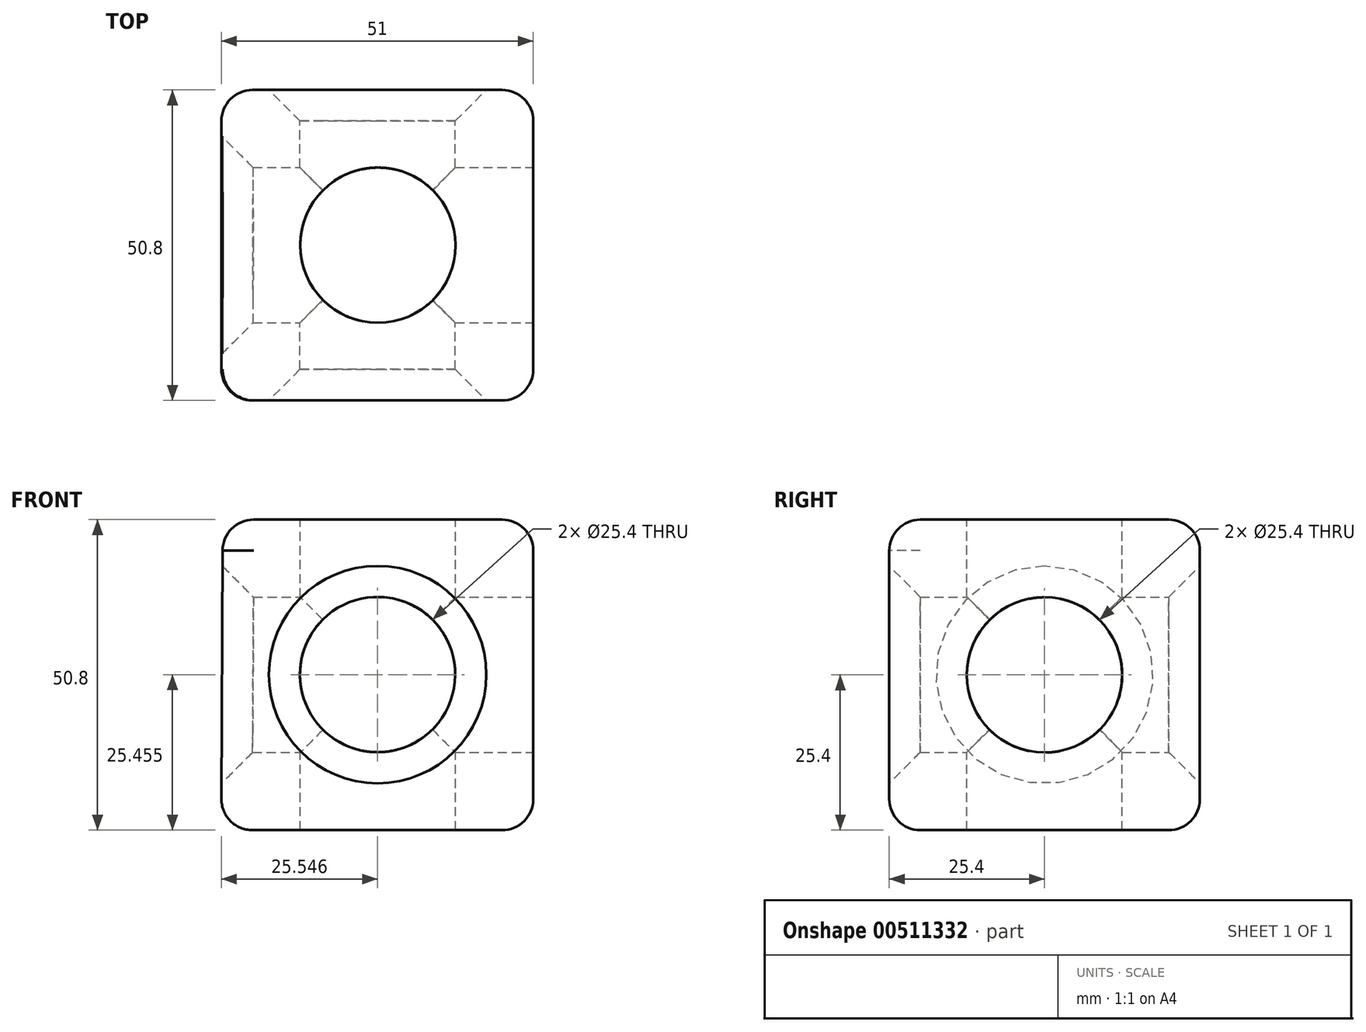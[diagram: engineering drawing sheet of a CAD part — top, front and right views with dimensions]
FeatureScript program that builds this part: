
annotation { "Feature Type Name" : "Feature", "Feature Type Description" : "" }
export const myFeature = defineFeature(function(context is Context, id is Id, definition is map)
    precondition{}
    {
        {
            var Q0;
            Q0=qCreatedBy(makeId("Front.planeOp"),FACE);
            var sketch = newSketch(context, id + "F0", { "sketchPlane" : qUnion([Q0])});
            skLineSegment(sketch, "E0", {"start": v(0, 0) * mm, "end": v(51.02, 0) * mm});
            skLineSegment(sketch, "E1", {"start": v(51.02, 0) * mm, "end": v(51.02, 50.8) * mm});
            skLineSegment(sketch, "E2", {"start": v(51.02, 50.8) * mm, "end": v(0.22, 50.8) * mm});
            skLineSegment(sketch, "E3", {"start": v(0.22, 50.8) * mm, "end": v(0, 0) * mm});
            skCircle(sketch, "E4", {"center": v(25.57, 25.46) * mm, "radius": 12.7 * mm});
            skSolve(sketch);
        }
        {
            var Q0;
            Q0 = qSketchRegion(id + "F0", true);
            extrude(context, id + "F1", {"entities" : qUnion([Q0]), "depth" : 50.8 * mm, "offsetDistance" : 25.4 * mm});
        }
        {
            var Q0;
            Q0=makeQuery(id+"F1.opExtrude","SWEPT_FACE",FACE,{"disambiguationData":[OSD([sQuery(id+"F0.wireOp",EDGE,"E2")])]});
            var sketch = newSketch(context, id + "F2", { "sketchPlane" : qUnion([Q0])});
            skCircle(sketch, "E5", {"center": v(25.62, -25.4) * mm, "radius": 12.7 * mm});
            skPoint(sketch, "E5.centerSnap0", {"position": v(51.02, -25.4) * mm});
            skPoint(sketch, "E5.centerSnap1", {"position": v(25.62, 0) * mm});
            skSolve(sketch);
        }
        {
            var Q0;
            Q0 = qSketchRegion(id + "F2", true);
            extrude(context, id + "F3", {"entities" : qUnion([Q0]), "operationType" : NewBodyOperationType.REMOVE, "oppositeDirection" : true, "depth" : 50.8 * mm, "offsetDistance" : 25.4 * mm});
        }
        {
            var Q0;
            Q0=makeQuery(id+"F1.opExtrude","SWEPT_FACE",FACE,{"disambiguationData":[OSD([sQuery(id+"F0.wireOp",EDGE,"E1")])]});
            var sketch = newSketch(context, id + "F4", { "sketchPlane" : qUnion([Q0])});
            skCircle(sketch, "E6", {"center": v(-25.4, 25.4) * mm, "radius": 12.7 * mm});
            skPoint(sketch, "E6.centerSnap0", {"position": v(-25.4, 50.8) * mm});
            skPoint(sketch, "E6.centerSnap1", {"position": v(0, 25.4) * mm});
            skSolve(sketch);
        }
        {
            var Q0;
            Q0 = qSketchRegion(id + "F4", true);
            extrude(context, id + "F5", {"entities" : qUnion([Q0]), "operationType" : NewBodyOperationType.REMOVE, "oppositeDirection" : true, "depth" : 558.8 * mm, "offsetDistance" : 25.4 * mm});
        }
        {
            var Q0;
            Q0=makeQuery(id+"F1.opExtrude","CAP_EDGE",EDGE,{"disambiguationData":[OSD([sQuery(id+"F0.wireOp",EDGE,"E2")])],"isStart":false});
            var Q1;
            Q1=makeQuery(id+"F1.opExtrude","SWEPT_EDGE",EDGE,{"disambiguationData":[OSD([sQuery(id+"F0.wireOp",EDGE,"E1"),sQuery(id+"F0.wireOp",EDGE,"E2")])]});
            var Q2;
            Q2=makeQuery(id+"F1.opExtrude","CAP_EDGE",EDGE,{"disambiguationData":[OSD([sQuery(id+"F0.wireOp",EDGE,"E2")])],"isStart":true});
            var Q3;
            Q3=makeQuery(id+"F1.opExtrude","SWEPT_EDGE",EDGE,{"disambiguationData":[OSD([sQuery(id+"F0.wireOp",EDGE,"E2"),sQuery(id+"F0.wireOp",EDGE,"E3")])]});
            var Q4;
            Q4=makeQuery(id+"F1.opExtrude","CAP_EDGE",EDGE,{"disambiguationData":[OSD([sQuery(id+"F0.wireOp",EDGE,"E1")])],"isStart":false});
            var Q5;
            Q5=makeQuery(id+"F1.opExtrude","SWEPT_EDGE",EDGE,{"disambiguationData":[OSD([sQuery(id+"F0.wireOp",EDGE,"E0"),sQuery(id+"F0.wireOp",EDGE,"E1")])]});
            var Q6;
            Q6=makeQuery(id+"F1.opExtrude","CAP_EDGE",EDGE,{"disambiguationData":[OSD([sQuery(id+"F0.wireOp",EDGE,"E0")])],"isStart":false});
            var Q7;
            Q7=makeQuery(id+"F1.opExtrude","CAP_EDGE",EDGE,{"disambiguationData":[OSD([sQuery(id+"F0.wireOp",EDGE,"E3")])],"isStart":false});
            var Q8;
            Q8=makeQuery(id+"F1.opExtrude","CAP_EDGE",EDGE,{"disambiguationData":[OSD([sQuery(id+"F0.wireOp",EDGE,"E1")])],"isStart":true});
            var Q9;
            Q9=makeQuery(id+"F1.opExtrude","CAP_EDGE",EDGE,{"disambiguationData":[OSD([sQuery(id+"F0.wireOp",EDGE,"E0")])],"isStart":true});
            var Q10;
            Q10=makeQuery(id+"F1.opExtrude","SWEPT_EDGE",EDGE,{"disambiguationData":[OSD([sQuery(id+"F0.wireOp",EDGE,"E0"),sQuery(id+"F0.wireOp",EDGE,"E3")])]});
            var Q11;
            Q11=makeQuery(id+"F1.opExtrude","CAP_EDGE",EDGE,{"disambiguationData":[OSD([sQuery(id+"F0.wireOp",EDGE,"E3")])],"isStart":true});
            fillet(context, id + "F6", {"entities" : qUnion([Q0, Q1, Q2, Q3, Q4, Q5, Q6, Q7, Q8, Q9, Q10, Q11]), "radius" : 5.08 * mm, "tangentPropagation" : true, "allowEdgeOverflow" : false});
        }
        {
            var Q0;
            Q0=makeQuery(id+"F3.boolean.opBoolean","COPY",EDGE,{"derivedFrom":makeQuery(id+"F3.opExtrude","CAP_EDGE",EDGE,{"disambiguationData":[OSD([sQuery(id+"F2.wireOp",EDGE,"E5")])],"isStart":true})});
            var Q1;
            Q1=makeQuery(id+"F1.opExtrude","CAP_EDGE",EDGE,{"disambiguationData":[OSD([sQuery(id+"F0.wireOp",EDGE,"E4")])],"isStart":false});
            var Q2;
            Q2=makeQuery(id+"F5.boolean.opBoolean","COPY",EDGE,{"derivedFrom":makeQuery(id+"F5.opExtrude","CAP_EDGE",EDGE,{"disambiguationData":[OSD([sQuery(id+"F4.wireOp",EDGE,"E6")])],"isStart":true})});
            var Q3;
            Q3=makeQuery(id+"F3.boolean.opBoolean","COPY",EDGE,{"derivedFrom":makeQuery(id+"F3.opExtrude","CAP_EDGE",EDGE,{"disambiguationData":[OSD([sQuery(id+"F2.wireOp",EDGE,"E5")])],"isStart":false})});
            var Q4;
            Q4=makeQuery(id+"F1.opExtrude","CAP_EDGE",EDGE,{"disambiguationData":[OSD([sQuery(id+"F0.wireOp",EDGE,"E4")])],"isStart":true});
            var Q5;
            Q5=makeQuery(id+"F5.boolean.opBoolean","INTERSECT",EDGE,{"derivedFrom":[makeQuery(id+"F1.opExtrude","SWEPT_FACE",FACE,{"disambiguationData":[OSD([sQuery(id+"F0.wireOp",EDGE,"E3")])]}),makeQuery(id+"F5.opExtrude","SWEPT_FACE",FACE,{"disambiguationData":[OSD([sQuery(id+"F4.wireOp",EDGE,"E6")])]})]});
            chamfer(context, id + "F7", {"entities" : qUnion([Q0, Q1, Q2, Q3, Q4, Q5]), "width" : 5.08 * mm, "tangentPropagation" : true});
        }
    });
